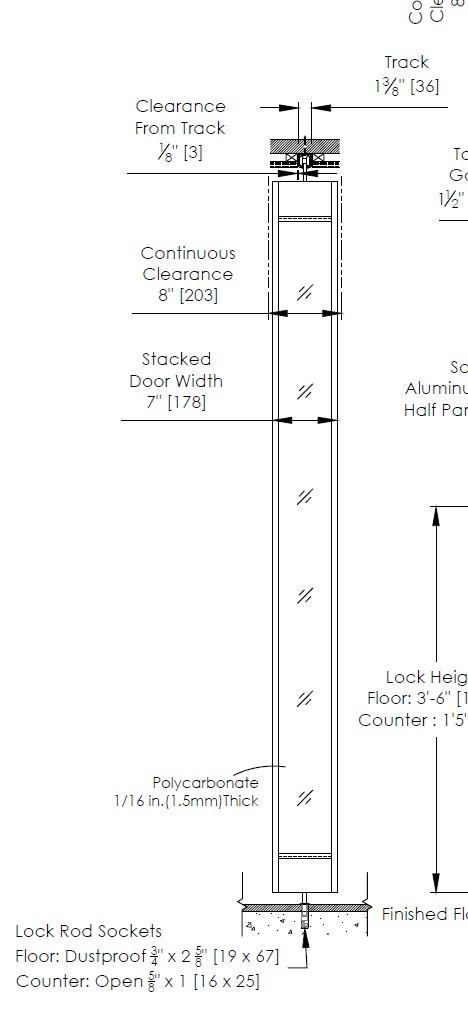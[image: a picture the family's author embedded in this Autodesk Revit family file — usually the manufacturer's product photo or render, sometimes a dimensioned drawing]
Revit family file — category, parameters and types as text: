
# Revit family: Side_Folding_Door_9100-CHI-EL_S126_S
name_source: partatom
category: Specialty Equipment
units: mm (PartAtom-declared; Revit-internal decimal feet)

## family parameters
Always vertical = Yes
Cut with Voids When Loaded = No
Enable Cutting in Views = No
Maintain Annotation Orientation = No
OmniClass Number = 23.30.10.21
OmniClass Title = Special Function Doors
Part Type = Normal
Room Calculation Point = No
Round Connector Dimension = Use Diameter
Shared = No
Work Plane-Based = No

## types (1)
- S-126-S
    Assembly Code = B2030420
    C Bottom Offset = 0' - 0 3/4"
    C Max Height = 14' - 0"
    C Max Width = 25' - 0"
    C Min Height = 4' - 0"
    C Min Width = 2' - 0"
    C Panel Width = 0' - 6"
    C Pocket Width = 0' - 8"
    C Top Gap = 0' - 1 1/2"
    C Track Height = 0' - 1 5/8"
    C Track Thickness = 0' - 0 1/8"
    C Track Width = 0' - 1 3/8"
    Constraints = 1
    Counter = Yes
    Default Elevation = 0' - 0"
    Description = Side-Folding Grille
    Floor = No
    Frame = Metal - Powder Coat - C.H.I Overhead Doors - White
    Glass = Glass - C.H.I Overhead Doors - Frosted
    Keynote = 08330
    Manufacturer = C.H.I. Overhead Doors
    Manufacturer Fax Number = 800-677-2650
    Model = S-126-S
    Product Documentation Link = Contact Manufacturer for More Information
    Product Page URL = Contact Manufacturer for More Information
    URL = https://www.chiohd.com
    Version = 2021-v1.a

## geometry (parser evidence)
native form markers: Sweep x19
no freeform markers — native parametric forms only
